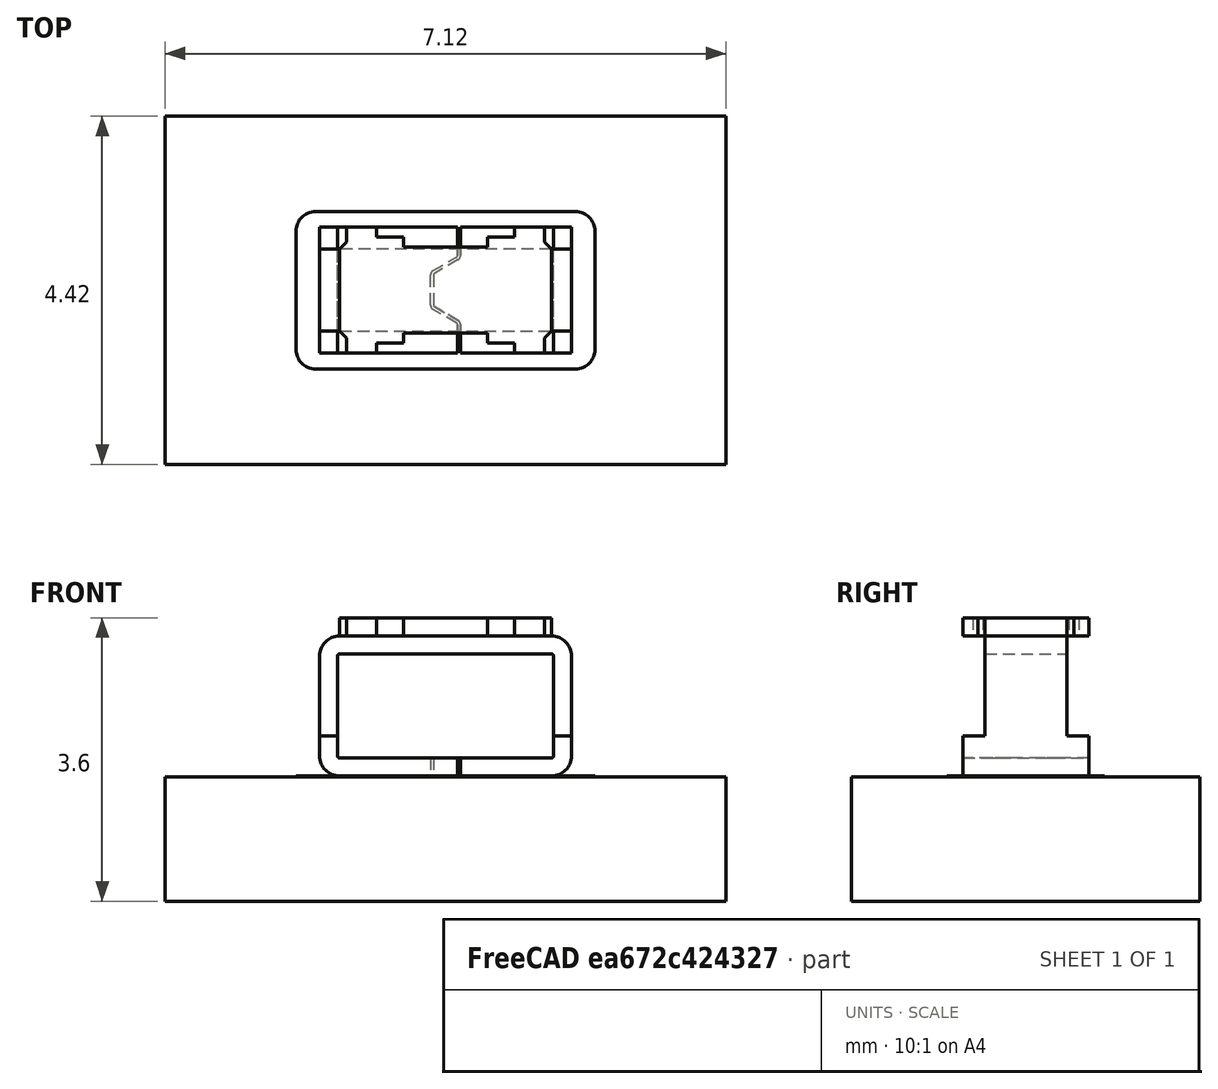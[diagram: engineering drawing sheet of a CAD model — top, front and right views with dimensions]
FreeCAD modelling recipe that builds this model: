
FCSTD DOCUMENT  (FreeCAD 1.0R39109 (Git))
Label: TestPoint_Keystone_5019_Miniature
License: All rights reserved
LicenseURL: http://en.wikipedia.org/wiki/All_rights_reserved
objects: Part::Feature×6, Sketcher::SketchObject×3, App::DocumentObjectGroup×1
note: 12 computed .brp shape members not serialized (recipe doc carries the construction recipe); baked Part::Feature solids carry a one-line shape summary decoded from their .brp

FEATURE [Part::Feature] Shape001  label="topPads"
  Placement = pos=(0,0,-0.01) rot=(0,0,1;0rad)
  shape: bbox 3.8 x 2 x 0.01 mm, 10 faces (baked)
FEATURE [Part::Feature] Shape  label="F.SilkS_outline_"
  Placement = pos=(0,0,0.01) rot=(0,0,1;0rad)
  shape: bbox 4.32 x 2.52 x 2e-07 mm, 0 faces, 0 solids (baked)
FEATURE [Sketcher::SketchObject] _F_SilkS__sketch  label="F.SilkS_"
  ArcFitTolerance = 1e-06
  FullyConstrained = false
  MakeInternals = false
  Placement = pos=(0,0,0.01) rot=(0,0,1;0rad)
  sketch-geometry (4):
    g0: LineSegment StartX=-2.1 StartY=1.2 StartZ=0 EndX=-2.1 EndY=-1.2 EndZ=0
    g1: LineSegment StartX=-2.1 StartY=-1.2 StartZ=0 EndX=2.1 EndY=-1.2 EndZ=0
    g2: LineSegment StartX=2.1 StartY=-1.2 StartZ=0 EndX=2.1 EndY=1.2 EndZ=0
    g3: LineSegment StartX=2.1 StartY=1.2 StartZ=0 EndX=-2.1 EndY=1.2 EndZ=0
  constraints (4):
    c: Coincident(g0,g1)
    c: Coincident(g1,g2)
    c: Coincident(g2,g3)
    c: Coincident(g3,g0)
FEATURE [Part::Feature] Shape002  label="F.CrtYd_outline_"
  Placement = pos=(0,0,0.01) rot=(0,0,1;0rad)
  shape: bbox 4.75 x 2.95 x 2e-07 mm, 0 faces, 0 solids (baked)
FEATURE [Sketcher::SketchObject] _F_CrtYd__sketch  label="F.CrtYd_"
  ArcFitTolerance = 1e-06
  FullyConstrained = false
  MakeInternals = false
  Placement = pos=(0,0,0.01) rot=(0,0,1;0rad)
  sketch-geometry (4):
    g0: LineSegment StartX=-2.35 StartY=1.45 StartZ=0 EndX=2.35 EndY=1.45 EndZ=0
    g1: LineSegment StartX=-2.35 StartY=-1.45 StartZ=0 EndX=-2.35 EndY=1.45 EndZ=0
    g2: LineSegment StartX=2.35 StartY=1.45 StartZ=0 EndX=2.35 EndY=-1.45 EndZ=0
    g3: LineSegment StartX=2.35 StartY=-1.45 StartZ=0 EndX=-2.35 EndY=-1.45 EndZ=0
FEATURE [Part::Feature] Shape003  label="F.Fab_outline_"
  Placement = pos=(0,0,0.01) rot=(0,0,1;0rad)
  shape: bbox 3.9 x 2.1 x 2e-07 mm, 0 faces, 0 solids (baked)
FEATURE [Sketcher::SketchObject] _F_Fab__sketch  label="F.Fab_"
  ArcFitTolerance = 1e-06
  FullyConstrained = false
  MakeInternals = false
  Placement = pos=(0,0,0.01) rot=(0,0,1;0rad)
  sketch-geometry (20):
    g0: LineSegment StartX=-1.9 StartY=0.5 StartZ=0 EndX=-1.9 EndY=-0.5 EndZ=0
    g1: LineSegment StartX=-1.9 StartY=-0.5 StartZ=0 EndX=1.9 EndY=-0.5 EndZ=0
    g2: LineSegment StartX=1.9 StartY=-0.5 StartZ=0 EndX=1.9 EndY=0.5 EndZ=0
    g3: LineSegment StartX=1.9 StartY=0.5 StartZ=0 EndX=-1.9 EndY=0.5 EndZ=0
    g4: LineSegment StartX=-1.25 StartY=1 StartZ=0 EndX=-1.25 EndY=0.5 EndZ=0
    g5: LineSegment StartX=-1.25 StartY=0.5 StartZ=0 EndX=0 EndY=0.5 EndZ=0
    g6: LineSegment StartX=0 StartY=0.5 StartZ=0 EndX=0 EndY=1 EndZ=0
    g7: LineSegment StartX=0 StartY=1 StartZ=0 EndX=-1.25 EndY=1 EndZ=0
    g8: LineSegment StartX=-1.25 StartY=-0.5 StartZ=0 EndX=-1.25 EndY=-1 EndZ=0
    g9: LineSegment StartX=-1.25 StartY=-1 StartZ=0 EndX=0 EndY=-1 EndZ=0
    g10: LineSegment StartX=0 StartY=-1 StartZ=0 EndX=0 EndY=-0.5 EndZ=0
    g11: LineSegment StartX=0 StartY=-0.5 StartZ=0 EndX=-1.25 EndY=-0.5 EndZ=0
    g12: LineSegment StartX=0 StartY=1 StartZ=0 EndX=0 EndY=0.5 EndZ=0
    g13: LineSegment StartX=0 StartY=0.5 StartZ=0 EndX=1.25 EndY=0.5 EndZ=0
    g14: LineSegment StartX=1.25 StartY=0.5 StartZ=0 EndX=1.25 EndY=1 EndZ=0
    g15: LineSegment StartX=1.25 StartY=1 StartZ=0 EndX=0 EndY=1 EndZ=0
    g16: LineSegment StartX=0 StartY=-0.5 StartZ=0 EndX=0 EndY=-1 EndZ=0
    g17: LineSegment StartX=0 StartY=-1 StartZ=0 EndX=1.25 EndY=-1 EndZ=0
    g18: LineSegment StartX=1.25 StartY=-1 StartZ=0 EndX=1.25 EndY=-0.5 EndZ=0
    g19: LineSegment StartX=1.25 StartY=-0.5 StartZ=0 EndX=0 EndY=-0.5 EndZ=0
  constraints (20):
    c: Coincident(g0,g1)
    c: Coincident(g1,g2)
    c: Coincident(g2,g3)
    c: Coincident(g3,g0)
    c: Coincident(g4,g5)
    c: Coincident(g5,g6)
    c: Coincident(g6,g7)
    c: Coincident(g7,g4)
    c: Coincident(g8,g9)
    c: Coincident(g9,g10)
    c: Coincident(g10,g11)
    c: Coincident(g11,g8)
    c: Coincident(g12,g13)
    c: Coincident(g13,g14)
    c: Coincident(g14,g15)
    c: Coincident(g15,g12)
    c: Coincident(g16,g17)
    c: Coincident(g17,g18)
    c: Coincident(g18,g19)
    c: Coincident(g19,g16)
FEATURE [Part::Feature] PCB
  shape: bbox 7.125 x 4.425 x 1.58 mm, 6 faces (baked)
FEATURE [App::DocumentObjectGroup] Group  label="TestPoint_Keystone_5019_Miniature-fp"
  Group = -> [Shape001,_F_SilkS__sketch,Shape,_F_CrtYd__sketch,Shape002,_F_Fab__sketch,Shape003,PCB]
FEATURE [Part::Feature] Shape011  label="RCWCTE"
  shape: bbox 3.2 x 1.6 x 2.007 mm, 76 faces (baked)
